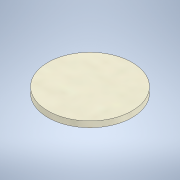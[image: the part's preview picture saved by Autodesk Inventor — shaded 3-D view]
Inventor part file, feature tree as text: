
AUTODESK INVENTOR PART (.ipt)
format: ipt  version: 2021 (Build 250183000, 183)  size: 97,792 bytes
history: native  units: mm
features: extrude x1, sketch x1
ambient origin geometry x8: Origin, YZ Plane, XZ Plane, XY Plane, X Axis, Y Axis, Z Axis, Center Point
bodies: Solid1 (feature_tree)
feature tree (2):
  extrude  "Extrusion1"  Depth=1.75mm TaperAngle=0.0deg
  sketch  "Sketch1"  dims[d0=25.1mm d1=1.75mm d2=0.0mm]
